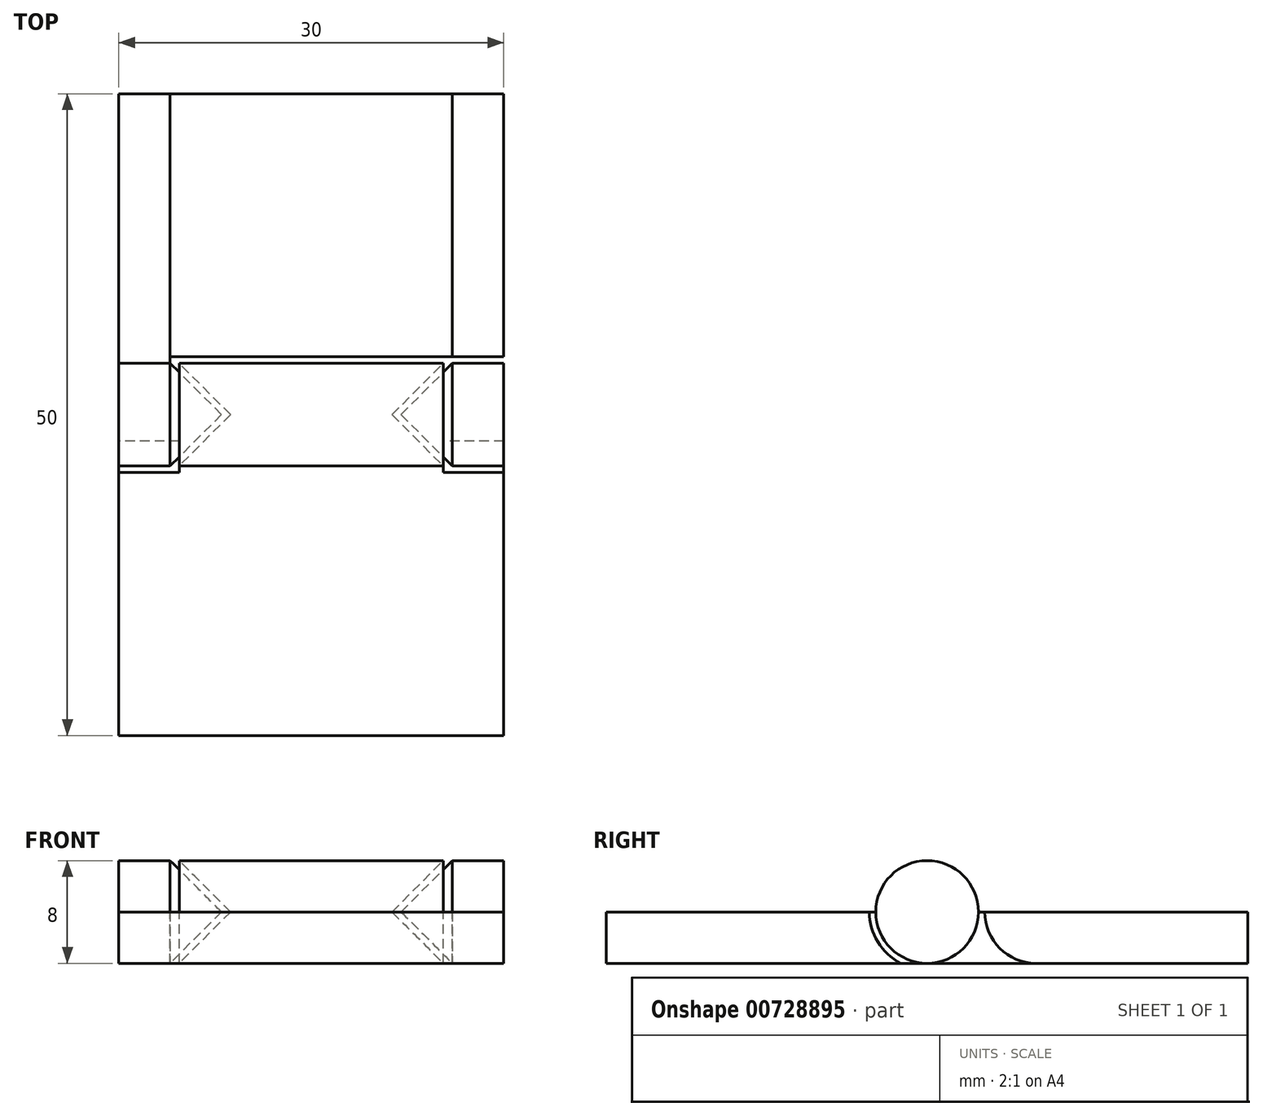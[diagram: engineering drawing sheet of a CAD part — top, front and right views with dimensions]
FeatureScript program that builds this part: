
annotation { "Feature Type Name" : "Feature", "Feature Type Description" : "" }
export const myFeature = defineFeature(function(context is Context, id is Id, definition is map)
    precondition{}
    {
        {
            var Q0;
            Q0=qCreatedBy(makeId("Top.planeOp"),FACE);
            var sketch = newSketch(context, id + "F0", { "sketchPlane" : qUnion([Q0])});
            skLineSegment(sketch, "E0", {"start": v(0, 0) * mm, "end": v(-6.3, 0) * mm});
            skLineSegment(sketch, "E1", {"start": v(-6.3, 0) * mm, "end": v(-10.3, 4) * mm});
            skLineSegment(sketch, "E2", {"start": v(-10.3, 4) * mm, "end": v(0, 4) * mm});
            skLineSegment(sketch, "E3", {"start": v(0, 4) * mm, "end": v(0, 0) * mm});
            skLineSegment(sketch, "E4", {"start": v(-7, 0) * mm, "end": v(-11, 4) * mm});
            skLineSegment(sketch, "E5", {"start": v(-11, 4) * mm, "end": v(-15, 4) * mm});
            skLineSegment(sketch, "E6", {"start": v(-15, 4) * mm, "end": v(-15, 0) * mm});
            skLineSegment(sketch, "E7", {"start": v(-15, 0) * mm, "end": v(-7, 0) * mm});
            skLineSegment(sketch, "E8.MirrorCS", {"start": v(11, 4) * mm, "end": v(15, 4) * mm});
            skLineSegment(sketch, "E9.MirrorCS", {"start": v(7, 0) * mm, "end": v(11, 4) * mm});
            skLineSegment(sketch, "E10.MirrorCS", {"start": v(15, 0) * mm, "end": v(7, 0) * mm});
            skLineSegment(sketch, "E11.MirrorCS", {"start": v(15, 4) * mm, "end": v(15, 0) * mm});
            skLineSegment(sketch, "E12.MirrorCS", {"start": v(6.3, 0) * mm, "end": v(10.3, 4) * mm});
            skLineSegment(sketch, "E13.MirrorCS", {"start": v(10.3, 4) * mm, "end": v(0, 4) * mm});
            skLineSegment(sketch, "E14.MirrorCS", {"start": v(0, 0) * mm, "end": v(6.3, 0) * mm});
            skSolve(sketch);
        }
        {
            var Q0;
            Q0=makeQuery(id+"F0.imprint","IMPRINT",FACE,{"disambiguationData":[TD([[makeQuery(id+"F0.imprint","IMPRINT",EDGE,{"derivedFrom":sQuery(id+"F0.wireOp",EDGE,"E4")}),1.0]])]});
            var Q1;
            Q1=makeQuery(id+"F0.imprint","IMPRINT",FACE,{"disambiguationData":[TD([[makeQuery(id+"F0.imprint","IMPRINT",EDGE,{"derivedFrom":sQuery(id+"F0.wireOp",EDGE,"E0")}),-1.0]])]});
            var Q2;
            Q2=makeQuery(id+"F0.imprint","IMPRINT",FACE,{"disambiguationData":[TD([[makeQuery(id+"F0.imprint","IMPRINT",EDGE,{"derivedFrom":sQuery(id+"F0.wireOp",EDGE,"E3")}),1.0]])]});
            var Q3;
            Q3=makeQuery(id+"F0.imprint","IMPRINT",FACE,{"disambiguationData":[TD([[makeQuery(id+"F0.imprint","IMPRINT",EDGE,{"derivedFrom":sQuery(id+"F0.wireOp",EDGE,"E8.MirrorCS")}),-1.0]])]});
            var Q4;
            Q4=sQuery(id+"F0.wireOp",EDGE,"E0");
            revolve(context, id + "F1", {"entities" : qUnion([Q0, Q1, Q2, Q3]), "axis" : qUnion([Q4]), "revolveType" : RevolveType.FULL});
        }
        {
            var Q0;
            Q0=qCreatedBy(makeId("Front.planeOp"),FACE);
            cPlane(context, id + "F2", {"entities" : qUnion([Q0]), "cplaneType" : CPlaneType.OFFSET, "offset" : 25 * mm, "width" : 150 * mm, "height" : 150 * mm});
        }
        {
            var Q0;
            Q0=qCreatedBy(makeId("Front.planeOp"),FACE);
            cPlane(context, id + "F3", {"entities" : qUnion([Q0]), "cplaneType" : CPlaneType.OFFSET, "offset" : 25 * mm, "oppositeDirection" : true, "width" : 150 * mm, "height" : 150 * mm});
        }
        {
            var Q0;
            Q0=qCreatedBy(id+"F2.planeOp",FACE);
            var sketch = newSketch(context, id + "F4", { "sketchPlane" : qUnion([Q0])});
            skLineSegment(sketch, "E15", {"start": v(10.3, -4) * mm, "end": v(-10.3, -4) * mm});
            skLineSegment(sketch, "E16", {"start": v(-10.3, 4) * mm, "end": v(10.3, 4) * mm});
            skLineSegment(sketch, "E17.0", {"start": v(-10.3, 4) * mm, "end": v(-10.3, -4) * mm});
            skLineSegment(sketch, "E18.0", {"start": v(10.3, 4) * mm, "end": v(10.3, -4) * mm});
            skSolve(sketch);
        }
        {
            var Q0;
            Q0=qSketchRegion(id+"F4",true);
            var Q1;
            Q1=makeQuery(id+"F1.opRevolve","SWEPT_FACE",FACE,{"disambiguationData":[OSD([sQuery(id+"F0.wireOp",EDGE,"E2"),sQuery(id+"F0.wireOp",EDGE,"E13.MirrorCS")])]});
            extrude(context, id + "F5", {"entities" : qUnion([Q0]), "operationType" : NewBodyOperationType.ADD, "endBound" : BoundingType.UP_TO_SURFACE, "oppositeDirection" : true, "endBoundEntityFace" : qUnion([Q1]), "depth" : 25 * mm});
        }
        {
            var Q0;
            Q0=qCreatedBy(id+"F3.planeOp",FACE);
            var sketch = newSketch(context, id + "F6", { "sketchPlane" : qUnion([Q0])});
            skLineSegment(sketch, "E19", {"start": v(15, -4) * mm, "end": v(11, -4) * mm});
            skLineSegment(sketch, "E20", {"start": v(11, 4) * mm, "end": v(15, 4) * mm});
            skLineSegment(sketch, "E21", {"start": v(-11, -4) * mm, "end": v(-15, -4) * mm});
            skLineSegment(sketch, "E22", {"start": v(-15, 4) * mm, "end": v(-11, 4) * mm});
            skLineSegment(sketch, "E23.0", {"start": v(-11, 4) * mm, "end": v(-11, -4) * mm});
            skLineSegment(sketch, "E24.0", {"start": v(-15, 4) * mm, "end": v(-15, -4) * mm});
            skLineSegment(sketch, "E25.0", {"start": v(11, 4) * mm, "end": v(11, -4) * mm});
            skLineSegment(sketch, "E26.0", {"start": v(15, 4) * mm, "end": v(15, -4) * mm});
            skSolve(sketch);
        }
        {
            var Q0;
            Q0=makeQuery(id+"F6.imprint","IMPRINT",FACE,{"disambiguationData":[TD([[makeQuery(id+"F6.imprint","IMPRINT",EDGE,{"derivedFrom":sQuery(id+"F6.wireOp",EDGE,"E19")}),-1.0]])]});
            var Q1;
            Q1=makeQuery(id+"F6.imprint","IMPRINT",FACE,{"disambiguationData":[TD([[makeQuery(id+"F6.imprint","IMPRINT",EDGE,{"derivedFrom":sQuery(id+"F6.wireOp",EDGE,"E21")}),-1.0]])]});
            extrude(context, id + "F7", {"entities" : qUnion([Q0, Q1]), "operationType" : NewBodyOperationType.ADD, "endBound" : BoundingType.UP_TO_NEXT, "depth" : 25 * mm, "offsetDistance" : 25 * mm});
        }
        {
            var Q0;
            Q0=makeQuery(id+"F7.opExtrude","SWEPT_FACE",FACE,{"disambiguationData":[OSD([sQuery(id+"F6.wireOp",EDGE,"E23.0")])]});
            var Q1;
            Q1=makeQuery(id+"F7.opExtrude","SWEPT_FACE",FACE,{"disambiguationData":[OSD([sQuery(id+"F6.wireOp",EDGE,"E25.0")])]});
            var Q2;
            Q2=makeQuery(id+"F1.opRevolve","SWEPT_BODY",BODY,{"disambiguationData":[OSD([sQuery(id+"F0.wireOp",EDGE,"E8.MirrorCS"),sQuery(id+"F0.wireOp",EDGE,"E9.MirrorCS"),sQuery(id+"F0.wireOp",EDGE,"E11.MirrorCS"),sQuery(id+"F0.wireOp",EDGE,"E10.MirrorCS")])]});
            extrude(context, id + "F8", {"entities" : qUnion([Q0]), "endBound" : BoundingType.UP_TO_SURFACE, "depth" : 6 * mm, "endBoundEntityFace" : qUnion([Q1]), "endBoundEntityBody" : qUnion([Q2]), "offsetDistance" : 25 * mm});
        }
        {
            var Q0;
            Q0=makeQuery(id+"F8.opExtrude","CAP_FACE",FACE,{"disambiguationData":[OSD([sQuery(id+"F6.wireOp",EDGE,"E23.0")])],"isStart":true});
            var sketch = newSketch(context, id + "F9", { "sketchPlane" : qUnion([Q0])});
            skArc(sketch, "E27.0", {"start": v(0, -4) * mm, "mid": v(-4, 0) * mm, "end": v(0, 4) * mm});
            skLineSegment(sketch, "E28", {"start": v(-4.25, 4) * mm, "end": v(-4.25, -4) * mm, "construction": true});
            skArc(sketch, "E29.MirrorCS", {"start": v(-8.5, -4) * mm, "mid": v(-4.5, 0) * mm, "end": v(-8.5, 4) * mm});
            skSolve(sketch);
        }
        {
            var Q0;
            {var subQ0=sQuery(id+"F9.wireOp",EDGE,"E27.0");Q0=makeQuery(id+"F9.imprint","IMPRINT",FACE,{"disambiguationData":[TD([[makeQuery(id+"F9.imprint","IMPRINT",EDGE,{"derivedFrom":subQ0}),1.0]])]});}
            extrude(context, id + "F10", {"entities" : qUnion([Q0]), "operationType" : NewBodyOperationType.REMOVE, "endBound" : BoundingType.THROUGH_ALL, "oppositeDirection" : true, "depth" : 25 * mm, "offsetDistance" : 25 * mm});
        }
        {
            var Q0;
            Q0=makeQuery(id+"F7.opExtrude","SWEPT_FACE",FACE,{"disambiguationData":[OSD([sQuery(id+"F6.wireOp",EDGE,"E23.0")])]});
            var sketch = newSketch(context, id + "F11", { "sketchPlane" : qUnion([Q0])});
            skLineSegment(sketch, "E30", {"start": v(25, 0) * mm, "end": v(4, 0) * mm});
            skSolve(sketch);
        }
        {
            var Q0;
            Q0=makeQuery(id+"F5.opExtrude","SWEPT_FACE",FACE,{"disambiguationData":[OSD([sQuery(id+"F4.wireOp",EDGE,"E18.0")])]});
            var sketch = newSketch(context, id + "F12", { "sketchPlane" : qUnion([Q0])});
            skLineSegment(sketch, "E31", {"start": v(-25, 0) * mm, "end": v(-4, 0) * mm});
            skArc(sketch, "E32.0", {"start": v(-4.5, 0) * mm, "mid": v(-3.18, -3.18) * mm, "end": v(0, -4.5) * mm});
            skSolve(sketch);
        }
        {
            var Q0;
            {var subQ0=sQuery(id+"F11.wireOp",EDGE,"E30");Q0=makeQuery(id+"F11.imprint","IMPRINT",FACE,{"disambiguationData":[TD([[makeQuery(id+"F11.imprint","IMPRINT",EDGE,{"derivedFrom":subQ0}),-1.0]])]});}
            var Q1;
            Q1=makeQuery(id+"F7.boolean.opBoolean","MERGE",FACE,{"derivedFrom":[makeQuery(id+"F1.opRevolve","SWEPT_FACE",FACE,{"disambiguationData":[OSD([sQuery(id+"F0.wireOp",EDGE,"E6")])]}),makeQuery(id+"F7.opExtrude","SWEPT_FACE",FACE,{"disambiguationData":[OSD([sQuery(id+"F6.wireOp",EDGE,"E24.0")])]})]});
            var Q2;
            Q2=makeQuery(id+"F7.boolean.opBoolean","MERGE",FACE,{"derivedFrom":[makeQuery(id+"F1.opRevolve","SWEPT_FACE",FACE,{"disambiguationData":[OSD([sQuery(id+"F0.wireOp",EDGE,"E11.MirrorCS")])]}),makeQuery(id+"F7.opExtrude","SWEPT_FACE",FACE,{"disambiguationData":[OSD([sQuery(id+"F6.wireOp",EDGE,"E26.0")])]})]});
            extrude(context, id + "F13", {"entities" : qUnion([Q0]), "operationType" : NewBodyOperationType.REMOVE, "endBound" : BoundingType.UP_TO_SURFACE, "oppositeDirection" : true, "depth" : 25 * mm, "endBoundEntityFace" : qUnion([Q1]), "offsetDistance" : 25 * mm, "hasSecondDirection" : true, "secondDirectionBound" : SecondDirectionBoundingType.UP_TO_SURFACE, "secondDirectionOppositeDirection" : false, "secondDirectionDepth" : 25 * mm, "secondDirectionBoundEntityFace" : qUnion([Q2])});
        }
        {
            var Q0;
            {var subQ0=sQuery(id+"F12.wireOp",EDGE,"E31");Q0=makeQuery(id+"F12.imprint","IMPRINT",FACE,{"disambiguationData":[TD([[makeQuery(id+"F12.imprint","IMPRINT",EDGE,{"derivedFrom":subQ0}),1.0]])]});}
            extrude(context, id + "F14", {"entities" : qUnion([Q0]), "operationType" : NewBodyOperationType.REMOVE, "endBound" : BoundingType.UP_TO_NEXT, "oppositeDirection" : true, "depth" : 25 * mm, "offsetDistance" : 25 * mm});
        }
        {
            var Q0;
            {var subQ0=sQuery(id+"F12.wireOp",EDGE,"E31");var subQ1=sQuery(id+"F4.wireOp",EDGE,"E18.0");var subQ2=makeQuery(id+"F5.opExtrude","CAP_EDGE",EDGE,{"disambiguationData":[OSD([subQ1])],"isStart":true});var subQ3=makeQuery(id+"F12.imprint","INTERSECT",VERTEX,{"derivedFrom":[subQ2,subQ0]});Q0=makeQuery(id+"F12.imprint","IMPRINT",FACE,{"disambiguationData":[TD([[makeQuery(id+"F12.imprint","IMPRINT",EDGE,{"disambiguationData":[TD([[subQ3,-1.0]])],"derivedFrom":subQ0}),-1.0]])]});}
            var Q1;
            Q1=makeQuery(id+"F7.boolean.opBoolean","MERGE",FACE,{"derivedFrom":[makeQuery(id+"F1.opRevolve","SWEPT_FACE",FACE,{"disambiguationData":[OSD([sQuery(id+"F0.wireOp",EDGE,"E11.MirrorCS")])]}),makeQuery(id+"F7.opExtrude","SWEPT_FACE",FACE,{"disambiguationData":[OSD([sQuery(id+"F6.wireOp",EDGE,"E26.0")])]})]});
            var Q2;
            Q2=makeQuery(id+"F7.boolean.opBoolean","MERGE",FACE,{"derivedFrom":[makeQuery(id+"F1.opRevolve","SWEPT_FACE",FACE,{"disambiguationData":[OSD([sQuery(id+"F0.wireOp",EDGE,"E6")])]}),makeQuery(id+"F7.opExtrude","SWEPT_FACE",FACE,{"disambiguationData":[OSD([sQuery(id+"F6.wireOp",EDGE,"E24.0")])]})]});
            extrude(context, id + "F15", {"entities" : qUnion([Q0]), "operationType" : NewBodyOperationType.ADD, "endBound" : BoundingType.UP_TO_SURFACE, "depth" : 2.5 * mm, "endBoundEntityFace" : qUnion([Q1]), "offsetDistance" : 25 * mm, "hasSecondDirection" : true, "secondDirectionBound" : SecondDirectionBoundingType.UP_TO_SURFACE, "secondDirectionOppositeDirection" : true, "secondDirectionDepth" : 25 * mm, "secondDirectionBoundEntityFace" : qUnion([Q2])});
        }
    });
